# Revit family: HL_Трап для внутренних помещений_HL304
name_source: partatom
category: Instalační zařizovací předměty
revit_build: Autodesk Revit 2016 (Build: 20151007_0715(x64)
units: mm (PartAtom-declared; Revit-internal decimal feet)

## family parameters
Bod výpočtu místnosti = Ano
Kóta kulaté spojky = Použít průměr
Nadpis OmniClass = Deck Waste Water Drains
Ořezat dutým tvarem při načtení = Ne
Sdílené = Ano
Typ součásti = Normální
Vždy vertikální = Ano
Založené na pracovní rovině = Ne
Číslo OmniClass = 23.70.50.21.24.14

## types (2) — shared parameters
EAN = 9003076703043
Klíčová poznámka = HL304
Komentáře k typům = HL304 Трап для внутренних помещений DN50 горизонтальный с 3-мя входными отверстиями расположенными сбоку DN40, 123х123мм/115х115мм
Model = HL304
Popis = Трапы для внутренних помещений
Připojení CW = Ne
Připojení HW = Ne
Připojení odpadu = Ano
Připojení ventilace = Ne
URL = http://www.hutterer-lechner.com
Výrobce = HL Hutterer & Lechner GmbH
ВЕС = 0,81 [kg]
ВЫСОТА МОНТАЖА = 135 mm
МАКСИМАЛЬНАЯ НАГРУЗКА КЛАССА = K3 - 300 kg
МАТЕРИАЛ = PE
НАСАДКА = 12-70mm / 123x123mm / PP
НОМИНАЛЬНЫЙ ДИАМЕТР = 40 mm
ПРИЁМНОЕ ОТВЕРСТИЕ = 3 x DN40
ПРОИЗВОДИТЕЛЬНОСТЬ = 0,5 l/sec
ПРОПУСКНАЯ СПОСОБНОСТЬ = 0.5 L/s
РАЗМЕР = DN50
РЕШЁТКА = 115x115mm / V2A

## type names (no varying parameters)
- HL304
- HL_Трап для внутренних помещений_HL304

## geometry (parser evidence)
native form markers: Sweep x64
no freeform markers — native parametric forms only
